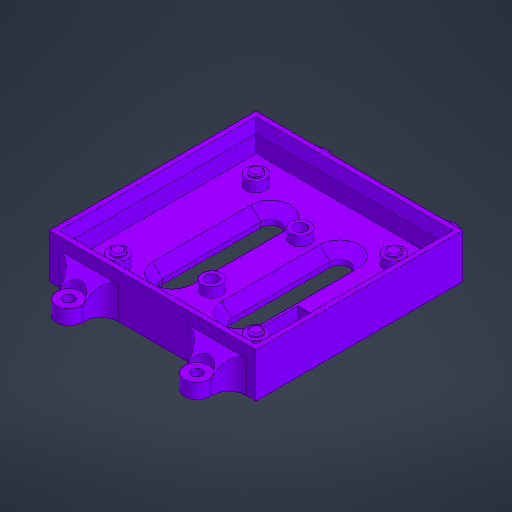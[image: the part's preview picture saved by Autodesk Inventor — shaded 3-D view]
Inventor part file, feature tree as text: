
AUTODESK INVENTOR PART (.ipt)
format: ipt  version: 2025.1 (Build 291241000, 241)  size: 877,056 bytes
history: native  units: mm
features: extrude x8, chamfer x5, sketch x4, mirror x4, fillet x1
ambient origin geometry x8: Origin, YZ Plane, XZ Plane, XY Plane, X Axis, Y Axis, Z Axis, Center Point
bodies: Solid1 (feature_tree)
feature tree (22):
  sketch  "Sketch1"  dims[d0=42.0mm d1=42.0mm d2=9.0mm d3=2.5mm d4=2.5mm d5=9.0mm d6=9.0mm d7=2.6mm d8=2.6mm d9=2.6mm d10=2.6mm d11=28.0mm d12=3.0mm d13=0.0mm]
  extrude  "Extrusion1"  Depth=3.0mm TaperAngle=0.0deg
  extrude  "Extrusion2"  Depth=4.0mm
  extrude  "Extrusion3"  Depth=4.0mm
  extrude  "Extrusion4"  Depth=4.0mm
  chamfer  "Chamfer1"  Distance=8.0mm
  sketch  "Sketch4"  dims[d16=4.0mm d17=4.0mm]
  extrude  "Extrusion6"  Depth=4.0mm
  mirror  "Mirror1"
  mirror  "Mirror4"
  chamfer  "Chamfer4"  Distance=2.0mm
  extrude  "Extrusion8"  Depth=2.0mm
  mirror  "Mirror5"
  mirror  "Mirror6"
  chamfer  "Chamfer5"  Distance=3.0mm
  fillet  "Fillet5"  Radius=1.5mm
  extrude  "Extrusion9"  Depth=6.0mm TaperAngle=0.0deg
  chamfer  "Chamfer6"  Distance=4.2mm
  extrude  "Extrusion10"  Depth=4.2mm
  chamfer  "Chamfer7"  Distance=2.75mm
  sketch  "Sketch2"  dims[d14=4.0mm d15=4.0mm]
  sketch  "Sketch5"  dims[d18=4.0mm d19=4.0mm d20=8.0mm d21=4.0mm d24=2.0mm d25=0.0mm d26=11.5mm d27=3.0mm d28=1.5mm d29=6.0mm d30=0.0mm d31=4.2mm d32=1.9mm d33=4.2mm d34=1.9mm d35=2.75mm d36=0.0mm d37=0.9mm d38=2.0mm d39=45.0deg d59=2.2mm d61=5.0mm d63=25.0mm d65=10.0mm d66=0.0mm d67=8.0mm d77=3.5mm d78=2.0mm d79=45.0deg d80=0.0mm d81=0.0mm d82=0.5mm d83=2.5mm d84=45.0deg d85=3.5mm d86=0.6mm d87=0.0mm d88=0.3mm d89=2.0mm d90=45.0deg d91=20.0mm d92=4.0mm d93=7.0mm d94=0.0mm d95=0.0mm d97=6.0mm d98=2.0mm d99=2.0mm d100=45.0deg]
